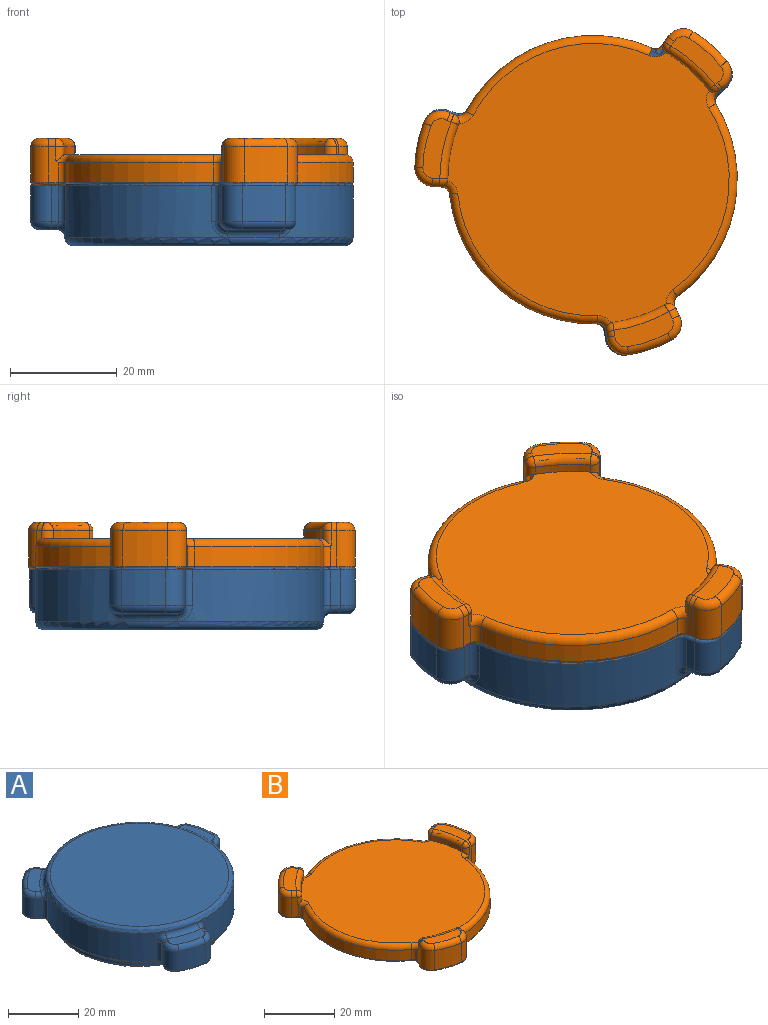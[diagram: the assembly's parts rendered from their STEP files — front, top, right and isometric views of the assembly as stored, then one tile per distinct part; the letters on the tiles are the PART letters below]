
ASSEMBLY  parts=2 mates=1
PART A: 103 faces, bbox 63x62.5x14.7 mm
  f0: cylinder r=27mm len=39.91mm, axis (0,0,1), area 396.5mm2, adj f45,f68,f69,f85,f88,f96
  f1: cylinder r=27mm len=38.76mm, axis (0,0,1), area 396.5mm2, adj f56,f73,f76,f92,f93,f96
  f2: plane 6.7x1.76mm, normal (-0.33,0.94,0), area 12.5mm2, adj f3,f54,f73,f74
  f3: cylinder r=3.5mm len=6.7mm, axis (0,0,-1), area 36mm2, adj f2,f4,f52,f72
  f4: cylinder r=24.41mm len=8.27mm, axis (0,0,-1), area 56.9mm2, adj f3,f5,f50,f75
  f5: cylinder r=3.5mm len=6.7mm, axis (0,0,-1), area 40.2mm2, adj f4,f6,f48,f77
  f6: plane 6.7x1.25mm, normal (0.08,-1,0), area 8.4mm2, adj f5,f46,f79,f81
  f7: plane 11.21x5.6mm, normal (0,0,1), area 38.3mm2, adj f72,f74,f75,f77,f78,f79
  f8: plane 60x59.37mm, normal (0,0,-1), area 386.4mm2, adj f26,f39,f40,f41,f42,f43,f44,f45
  f9: cylinder r=2.15mm len=8mm, axis (0,0,-1), area 108.1mm2, adj f10,f98
  f10: plane 4.3x4.3mm, normal (0,0,-1), area 14.5mm2, adj f9
  f11: cylinder r=2.15mm len=8mm, axis (0,0,-1), area 108.1mm2, adj f12,f97
  f12: plane 4.3x4.3mm, normal (0,0,-1), area 14.5mm2, adj f11
  f13: cylinder r=27mm len=30.36mm, axis (0,0,1), area 396.5mm2, adj f44,f61,f64,f80,f81,f96
  f14: plane 6.7x1.41mm, normal (-0.65,-0.76,0), area 12.5mm2, adj f15,f47,f85,f86
  f15: cylinder r=3.5mm len=6.7mm, axis (0,0,-1), area 36mm2, adj f14,f16,f49,f84
  f16: cylinder r=24.41mm len=6.7mm, axis (0,0,-1), area 56.9mm2, adj f15,f17,f51,f87
  f17: cylinder r=3.5mm len=6.7mm, axis (0,0,-1), area 40.2mm2, adj f16,f18,f53,f89
  f18: plane 6.7x1.04mm, normal (0.83,0.56,0), area 8.4mm2, adj f17,f55,f91,f93
  f19: plane 9.91x9.39mm, normal (0,0,1), area 38.3mm2, adj f84,f86,f87,f89,f90,f91
  f20: cylinder r=2.15mm len=8mm, axis (0,0,-1), area 108.1mm2, adj f21,f101
  f21: plane 4.3x4.3mm, normal (0,0,-1), area 14.5mm2, adj f20
  f22: cylinder r=2.15mm len=8mm, axis (0,0,-1), area 108.1mm2, adj f23,f102
  f23: plane 4.3x4.3mm, normal (0,0,-1), area 14.5mm2, adj f22
  f24: cylinder r=23mm len=46mm, axis (0,0,1), area 1242.8mm2, adj f57,f95
  f25: plane 49x49mm, normal (0,0,-1), area 150.8mm2, adj f57,f58
  f26: cylinder r=25mm len=50mm, axis (0,0,1), area 392.7mm2, adj f8,f58
  f27: plane 51x51mm, normal (0,0,1), area 2042.8mm2, adj f96
  f28: plane 40x40mm, normal (0,0,-1), area 1256.6mm2, adj f95
  f29: plane 6.7x1.83mm, normal (0.98,-0.19,0), area 12.5mm2, adj f30,f42,f61,f62
  f30: cylinder r=3.5mm len=6.7mm, axis (0,0,-1), area 36mm2, adj f29,f31,f40,f60
  f31: cylinder r=24.41mm len=8.04mm, axis (0,0,-1), area 56.9mm2, adj f30,f32,f39,f63
  f32: cylinder r=3.5mm len=6.7mm, axis (0,0,-1), area 40.2mm2, adj f31,f33,f41,f65
  f33: plane 6.7x1.13mm, normal (-0.9,0.43,0), area 8.4mm2, adj f32,f43,f67,f69
  f34: plane 11.2x6.49mm, normal (0,0,1), area 38.3mm2, adj f60,f62,f63,f65,f66,f67
  f35: cylinder r=2.15mm len=8mm, axis (0,0,-1), area 108.1mm2, adj f36,f100
  f36: plane 4.3x4.3mm, normal (0,0,-1), area 14.5mm2, adj f35
  f37: cylinder r=2.15mm len=8mm, axis (0,0,-1), area 108.1mm2, adj f38,f99
  f38: plane 4.3x4.3mm, normal (0,0,-1), area 14.5mm2, adj f37
  f39: torus R=23.91mm, axis (0,0,-1), area 6.6mm2, adj f8,f31,f40,f41
  f40: torus R=3mm, axis (0,0,-1), area 4mm2, adj f8,f30,f39,f42
  f41: torus R=3mm, axis (0,0,-1), area 4.5mm2, adj f8,f32,f39,f43
  f42: cylinder r=0.5mm len=3.64mm, axis (-0.19,-0.98,0), area 2.1mm2, adj f8,f29,f40,f59
  f43: cylinder r=0.5mm len=2.96mm, axis (0.43,0.9,0), area 1.7mm2, adj f8,f33,f41,f70
  f44: torus R=26.5mm, axis (0,0,-1), area 32.9mm2, adj f8,f13,f59,f82
  f45: torus R=26.5mm, axis (0,0,-1), area 32.9mm2, adj f0,f8,f70,f83
  f46: cylinder r=0.5mm len=3.08mm, axis (-1,-0.08,0), area 1.7mm2, adj f6,f8,f48,f82
  f47: cylinder r=0.5mm len=3.06mm, axis (-0.76,0.65,0), area 2.1mm2, adj f8,f14,f49,f83
  f48: torus R=3mm, axis (0,0,-1), area 4.5mm2, adj f5,f8,f46,f50
  f49: torus R=3mm, axis (0,0,-1), area 4mm2, adj f8,f15,f47,f51
  f50: torus R=23.91mm, axis (0,0,-1), area 6.6mm2, adj f4,f8,f48,f52
  f51: torus R=23.91mm, axis (0,0,-1), area 6.6mm2, adj f8,f16,f49,f53
  f52: torus R=3mm, axis (0,0,-1), area 4mm2, adj f3,f8,f50,f54
  f53: torus R=3mm, axis (0,0,-1), area 4.5mm2, adj f8,f17,f51,f55
  f54: cylinder r=0.5mm len=3.57mm, axis (0.94,0.33,0), area 2.1mm2, adj f2,f8,f52,f71
  f55: cylinder r=0.5mm len=2.8mm, axis (0.56,-0.83,0), area 1.7mm2, adj f8,f18,f53,f94
  f56: torus R=26.5mm, axis (0,0,-1), area 32.9mm2, adj f1,f8,f71,f94
  f57: torus R=23.5mm, axis (0,0,-1), area 114.4mm2, adj f24,f25
  f58: torus R=24.5mm, axis (0,0,-1), area 122.5mm2, adj f25,f26
  f59: bspline ~1.81x1.67mm, area 1.4mm2, adj f42,f44,f61
  f60: torus R=2mm, axis (0,0,-1), area 10.7mm2, adj f30,f34,f62,f63
  f61: cylinder r=1.5mm len=6.7mm, axis (0,0,1), area 14.1mm2, adj f13,f29,f59,f64
  f62: cylinder r=1.5mm len=2.11mm, axis (0.19,0.98,0), area 4mm2, adj f29,f34,f60,f64
  f63: torus R=22.91mm, axis (0,0,-1), area 19.6mm2, adj f31,f34,f60,f65
  f64: bspline ~3.52x3.48mm, area 7.1mm2, adj f13,f61,f62,f66
  f65: torus R=2mm, axis (0,0,-1), area 12.1mm2, adj f32,f34,f63,f67
  f66: torus R=28.5mm, axis (0,0,-1), area 24.8mm2, adj f34,f64,f68,f96
  f67: cylinder r=1.5mm len=1.96mm, axis (-0.43,-0.9,0), area 2.7mm2, adj f33,f34,f65,f68
  f68: bspline ~3.67x2.96mm, area 7.1mm2, adj f0,f66,f67,f69
  f69: cylinder r=1.5mm len=6.7mm, axis (0,0,1), area 14.1mm2, adj f0,f33,f68,f70
  f70: bspline ~1.88x1.7mm, area 1.4mm2, adj f43,f45,f69
  f71: bspline ~1.81x1.74mm, area 1.4mm2, adj f54,f56,f73
  f72: torus R=2mm, axis (0,0,-1), area 10.7mm2, adj f3,f7,f74,f75
  f73: cylinder r=1.5mm len=6.7mm, axis (0,0,1), area 14.1mm2, adj f1,f2,f71,f76
  f74: cylinder r=1.5mm len=2.26mm, axis (-0.94,-0.33,0), area 4mm2, adj f2,f7,f72,f76
  f75: torus R=22.91mm, axis (0,0,-1), area 19.6mm2, adj f4,f7,f72,f77
  f76: bspline ~3.52x3.16mm, area 7.1mm2, adj f1,f73,f74,f78
  f77: torus R=2mm, axis (0,0,-1), area 12.1mm2, adj f5,f7,f75,f79
  f78: torus R=28.5mm, axis (0,0,-1), area 24.8mm2, adj f7,f76,f80,f96
  f79: cylinder r=1.5mm len=1.6mm, axis (1,0.08,0), area 2.7mm2, adj f6,f7,f77,f80
  f80: bspline ~3.67x3.33mm, area 7.1mm2, adj f13,f78,f79,f81
  f81: cylinder r=1.5mm len=6.7mm, axis (0,0,1), area 14.1mm2, adj f6,f13,f80,f82
  f82: bspline ~1.78x1.73mm, area 0.7mm2, adj f44,f46,f81
  f83: bspline ~1.91x1.65mm, area 0.7mm2, adj f45,f47,f85
  f84: torus R=2mm, axis (0,0,-1), area 10.7mm2, adj f15,f19,f86,f87
  f85: cylinder r=1.5mm len=6.7mm, axis (0,0,1), area 14.1mm2, adj f0,f14,f83,f88
  f86: cylinder r=1.5mm len=2.39mm, axis (0.76,-0.65,0), area 4mm2, adj f14,f19,f84,f88
  f87: torus R=22.91mm, axis (0,0,-1), area 19.6mm2, adj f16,f19,f84,f89
  f88: bspline ~3.55x3.52mm, area 7.1mm2, adj f0,f85,f86,f90
  f89: torus R=2mm, axis (0,0,-1), area 12.1mm2, adj f17,f19,f87,f91
  f90: torus R=28.5mm, axis (0,0,-1), area 24.8mm2, adj f19,f88,f92,f96
  f91: cylinder r=1.5mm len=2.03mm, axis (-0.56,0.83,0), area 2.7mm2, adj f18,f19,f89,f92
  f92: bspline ~3.67x3.52mm, area 7.1mm2, adj f1,f90,f91,f93
  f93: cylinder r=1.5mm len=6.7mm, axis (0,0,1), area 14.1mm2, adj f1,f18,f92,f94
  f94: bspline ~1.87x1.73mm, area 1.4mm2, adj f55,f56,f93
  f95: torus R=20mm, axis (0,0,1), area 648.7mm2, adj f24,f28
  f96: torus R=25.5mm, axis (0,0,1), area 391.6mm2, adj f0,f1,f13,f27,f66,f78,f90
  f97: torus R=2.35mm, axis (0,0,-1), area 4.4mm2, adj f8,f11
  f98: torus R=2.35mm, axis (0,0,-1), area 4.4mm2, adj f8,f9
  f99: torus R=2.35mm, axis (0,0,-1), area 4.4mm2, adj f8,f37
  f100: torus R=2.35mm, axis (0,0,-1), area 4.4mm2, adj f8,f35
  f101: torus R=2.35mm, axis (0,0,-1), area 4.4mm2, adj f8,f20
  f102: torus R=2.35mm, axis (0,0,-1), area 4.4mm2, adj f8,f22
PART B: 117 faces, bbox 63x62.5x8.7 mm
  f0: cylinder r=27mm len=27.4mm, axis (0,0,1), area 145.8mm2, adj f41,f44,f46,f61
  f1: cylinder r=27mm len=34.99mm, axis (0,0,1), area 145.8mm2, adj f55,f58,f60,f77
  f2: plane 49.6x49.6mm, normal (0,0,-1), area 1932.2mm2, adj f85
  f3: cylinder r=25.3mm len=50.6mm, axis (0,0,1), area 317.9mm2, adj f85,f86
  f4: plane 60x59.37mm, normal (0,0,-1), area 262.4mm2, adj f61,f62,f63,f64,f65,f66,f67,f68
  f5: cylinder r=27mm len=36.02mm, axis (0,0,1), area 145.8mm2, adj f47,f50,f53,f76
  f6: plane 52.72x52.72mm, normal (0,0,1), area 2103.6mm2, adj f7,f18,f29,f40,f42,f43,f44,f45
  f7: cylinder r=27mm len=7.64mm, axis (0,0,-1), area 16.5mm2, adj f6,f48,f54,f93
  f8: plane 6.7x1.42mm, normal (-0.65,-0.76,0), area 11.5mm2, adj f9,f47,f48,f49,f80,f92
  f9: cylinder r=3.5mm len=6.7mm, axis (0,0,-1), area 36mm2, adj f8,f10,f82,f90
  f10: cylinder r=24.41mm len=6.7mm, axis (0,0,-1), area 56.9mm2, adj f9,f11,f84,f88
  f11: cylinder r=3.5mm len=6.7mm, axis (0,0,-1), area 40.2mm2, adj f10,f12,f83,f87
  f12: plane 6.7x1.04mm, normal (0.83,0.56,0), area 7.4mm2, adj f11,f54,f55,f56,f81,f89
  f13: plane 9.91x9.39mm, normal (0,0,1), area 38.3mm2, adj f87,f88,f89,f90,f92,f93
  f14: cylinder r=2.15mm len=8mm, axis (0,0,-1), area 108.1mm2, adj f15,f116
  f15: plane 4.3x4.3mm, normal (0,0,-1), area 14.5mm2, adj f14
  f16: cylinder r=2.15mm len=8mm, axis (0,0,-1), area 108.1mm2, adj f17,f115
  f17: plane 4.3x4.3mm, normal (0,0,-1), area 14.5mm2, adj f16
  f18: cylinder r=27.2mm len=10.1mm, axis (0,0,-1), area 16.6mm2, adj f6,f40,f57,f100
  f19: plane 6.71x1.77mm, normal (-0.33,0.94,0), area 10.9mm2, adj f20,f57,f59,f60,f73,f96
  f20: cylinder r=3.5mm len=6.7mm, axis (0,0,-1), area 36mm2, adj f19,f21,f71,f95
  f21: cylinder r=24.41mm len=8.27mm, axis (0,0,-1), area 56.9mm2, adj f20,f22,f69,f97
  f22: cylinder r=3.5mm len=6.7mm, axis (0,0,-1), area 40.2mm2, adj f21,f23,f67,f99
  f23: plane 6.71x1.26mm, normal (0.08,-1,0), area 6.9mm2, adj f22,f40,f41,f42,f65,f101
  f24: plane 11.2x5.42mm, normal (0,0,1), area 36.2mm2, adj f95,f96,f97,f99,f100,f101
  f25: cylinder r=2.15mm len=8mm, axis (0,0,-1), area 108.1mm2, adj f26,f112
  f26: plane 4.3x4.3mm, normal (0,0,-1), area 14.5mm2, adj f25
  f27: cylinder r=2.15mm len=8mm, axis (0,0,-1), area 108.1mm2, adj f28,f111
  f28: plane 4.3x4.3mm, normal (0,0,-1), area 14.5mm2, adj f27
  f29: cylinder r=27.4mm len=9.86mm, axis (0,0,-1), area 16.7mm2, adj f6,f43,f51,f108
  f30: plane 6.73x1.86mm, normal (0.98,-0.19,0), area 10.4mm2, adj f31,f43,f45,f46,f64,f104
  f31: cylinder r=3.5mm len=6.7mm, axis (0,0,-1), area 36mm2, adj f30,f32,f66,f103
  f32: cylinder r=24.41mm len=8.04mm, axis (0,0,-1), area 56.9mm2, adj f31,f33,f68,f105
  f33: cylinder r=3.5mm len=6.7mm, axis (0,0,-1), area 40.2mm2, adj f32,f34,f70,f107
  f34: plane 6.73x1.16mm, normal (-0.9,0.43,0), area 6.4mm2, adj f33,f51,f52,f53,f72,f109
  f35: plane 11.13x6.12mm, normal (0,0,1), area 34mm2, adj f103,f104,f105,f107,f108,f109
  f36: cylinder r=2.15mm len=8mm, axis (0,0,-1), area 108.1mm2, adj f37,f114
  f37: plane 4.3x4.3mm, normal (0,0,-1), area 14.5mm2, adj f36
  f38: cylinder r=2.15mm len=8mm, axis (0,0,-1), area 108.1mm2, adj f39,f113
  f39: plane 4.3x4.3mm, normal (0,0,-1), area 14.5mm2, adj f38
  f40: cylinder r=1.5mm len=2.72mm, axis (0,0,-1), area 5mm2, adj f6,f18,f23,f42,f102
  f41: cylinder r=1.5mm len=3.6mm, axis (0,0,1), area 7.6mm2, adj f0,f23,f42,f63
  f42: torus R=3mm, axis (0,0,1), area 5.8mm2, adj f6,f23,f40,f41,f44
  f43: cylinder r=1.5mm len=2.58mm, axis (0,0,-1), area 5mm2, adj f6,f29,f30,f45,f106
  f44: torus R=25.5mm, axis (0,0,1), area 93.5mm2, adj f0,f6,f42,f45
  f45: torus R=3mm, axis (0,0,1), area 6.2mm2, adj f6,f30,f43,f44,f46
  f46: cylinder r=1.5mm len=3.6mm, axis (0,0,1), area 7.6mm2, adj f0,f30,f45,f62
  f47: cylinder r=1.5mm len=3.6mm, axis (0,0,1), area 7.6mm2, adj f5,f8,f49,f78
  f48: cylinder r=1.5mm len=2.86mm, axis (0,0,-1), area 5mm2, adj f6,f7,f8,f49,f94
  f49: torus R=3mm, axis (0,0,1), area 5.4mm2, adj f6,f8,f47,f48,f50
  f50: torus R=25.5mm, axis (0,0,1), area 93.5mm2, adj f5,f6,f49,f52
  f51: cylinder r=1.5mm len=2.59mm, axis (0,0,-1), area 5mm2, adj f6,f29,f34,f52,f110
  f52: torus R=3mm, axis (0,0,1), area 6.2mm2, adj f6,f34,f50,f51,f53
  f53: cylinder r=1.5mm len=3.6mm, axis (0,0,1), area 7.6mm2, adj f5,f34,f52,f74
  f54: cylinder r=1.5mm len=2.86mm, axis (0,0,-1), area 5mm2, adj f6,f7,f12,f56,f91
  f55: cylinder r=1.5mm len=3.6mm, axis (0,0,1), area 7.6mm2, adj f1,f12,f56,f79
  f56: torus R=3mm, axis (0,0,1), area 5.4mm2, adj f6,f12,f54,f55,f58
  f57: cylinder r=1.5mm len=2.72mm, axis (0,0,-1), area 5mm2, adj f6,f18,f19,f59,f98
  f58: torus R=25.5mm, axis (0,0,1), area 93.5mm2, adj f1,f6,f56,f59
  f59: torus R=3mm, axis (0,0,1), area 5.8mm2, adj f6,f19,f57,f58,f60
  f60: cylinder r=1.5mm len=3.6mm, axis (0,0,1), area 7.6mm2, adj f1,f19,f59,f75
  f61: torus R=26.5mm, axis (0,0,1), area 31.6mm2, adj f0,f4,f62,f63
  f62: torus R=2mm, axis (0,0,1), area 1.9mm2, adj f4,f46,f61,f64
  f63: torus R=2mm, axis (0,0,1), area 1.9mm2, adj f4,f41,f61,f65
  f64: cylinder r=0.5mm len=1.93mm, axis (0.19,0.98,0), area 1.5mm2, adj f4,f30,f62,f66
  f65: cylinder r=0.5mm len=1.33mm, axis (1,0.08,0), area 1mm2, adj f4,f23,f63,f67
  f66: torus R=3mm, axis (0,0,1), area 4mm2, adj f4,f31,f64,f68
  f67: torus R=3mm, axis (0,0,1), area 4.5mm2, adj f4,f22,f65,f69
  f68: torus R=23.91mm, axis (0,0,1), area 6.6mm2, adj f4,f32,f66,f70
  f69: torus R=23.91mm, axis (0,0,1), area 6.6mm2, adj f4,f21,f67,f71
  f70: torus R=3mm, axis (0,0,1), area 4.5mm2, adj f4,f33,f68,f72
  f71: torus R=3mm, axis (0,0,1), area 4mm2, adj f4,f20,f69,f73
  f72: cylinder r=0.5mm len=1.39mm, axis (-0.43,-0.9,0), area 1mm2, adj f4,f34,f70,f74
  f73: cylinder r=0.5mm len=1.93mm, axis (-0.94,-0.33,0), area 1.5mm2, adj f4,f19,f71,f75
  f74: torus R=2mm, axis (0,0,1), area 1.9mm2, adj f4,f53,f72,f76
  f75: torus R=2mm, axis (0,0,1), area 1.9mm2, adj f4,f60,f73,f77
  f76: torus R=26.5mm, axis (0,0,1), area 31.6mm2, adj f4,f5,f74,f78
  f77: torus R=26.5mm, axis (0,0,1), area 31.6mm2, adj f1,f4,f75,f79
  f78: torus R=2mm, axis (0,0,1), area 1.9mm2, adj f4,f47,f76,f80
  f79: torus R=2mm, axis (0,0,1), area 1.9mm2, adj f4,f55,f77,f81
  f80: cylinder r=0.5mm len=1.74mm, axis (0.76,-0.65,0), area 1.5mm2, adj f4,f8,f78,f82
  f81: cylinder r=0.5mm len=1.36mm, axis (-0.56,0.83,0), area 1mm2, adj f4,f12,f79,f83
  f82: torus R=3mm, axis (0,0,1), area 4mm2, adj f4,f9,f80,f84
  f83: torus R=3mm, axis (0,0,1), area 4.5mm2, adj f4,f11,f81,f84
  f84: torus R=23.91mm, axis (0,0,1), area 6.6mm2, adj f4,f10,f82,f83
  f85: torus R=24.8mm, axis (0,0,1), area 124mm2, adj f2,f3
  f86: torus R=25.8mm, axis (0,0,1), area 125.7mm2, adj f3,f4
  f87: torus R=2mm, axis (0,0,-1), area 12.1mm2, adj f11,f13,f88,f89
  f88: torus R=22.91mm, axis (0,0,-1), area 19.6mm2, adj f10,f13,f87,f90
  f89: cylinder r=1.5mm len=1.84mm, axis (-0.56,0.83,0), area 2.3mm2, adj f12,f13,f87,f91
  f90: torus R=2mm, axis (0,0,-1), area 10.7mm2, adj f9,f13,f88,f92
  f91: sphere r=1.5mm, area 3.7mm2, adj f54,f89,f93
  f92: cylinder r=1.5mm len=2.13mm, axis (0.76,-0.65,0), area 3.6mm2, adj f8,f13,f90,f94
  f93: torus R=28.5mm, axis (0,0,-1), area 24.8mm2, adj f7,f13,f91,f94
  f94: sphere r=1.5mm, area 3.7mm2, adj f48,f92,f93
  f95: torus R=2mm, axis (0,0,-1), area 10.7mm2, adj f20,f24,f96,f97
  f96: cylinder r=1.5mm len=1.85mm, axis (-0.94,-0.33,0), area 3.1mm2, adj f19,f24,f95,f98
  f97: torus R=22.91mm, axis (0,0,-1), area 19.6mm2, adj f21,f24,f95,f99
  f98: sphere r=1.5mm, area 3.7mm2, adj f57,f96,f100
  f99: torus R=2mm, axis (0,0,-1), area 12.1mm2, adj f22,f24,f97,f101
  f100: torus R=28.7mm, axis (0,0,-1), area 24.9mm2, adj f18,f24,f98,f102
  f101: cylinder r=1.5mm len=1.56mm, axis (1,0.08,0), area 1.9mm2, adj f23,f24,f99,f102
  f102: sphere r=1.5mm, area 3.6mm2, adj f40,f100,f101
  f103: torus R=2mm, axis (0,0,-1), area 10.7mm2, adj f31,f35,f104,f105
  f104: cylinder r=1.5mm len=1.68mm, axis (0.19,0.98,0), area 2.6mm2, adj f30,f35,f103,f106
  f105: torus R=22.91mm, axis (0,0,-1), area 19.6mm2, adj f32,f35,f103,f107
  f106: sphere r=1.5mm, area 3.7mm2, adj f43,f104,f108
  f107: torus R=2mm, axis (0,0,-1), area 12.1mm2, adj f33,f35,f105,f109
  f108: torus R=28.9mm, axis (0,0,-1), area 25.1mm2, adj f29,f35,f106,f110
  f109: cylinder r=1.5mm len=1.64mm, axis (-0.43,-0.9,0), area 1.4mm2, adj f34,f35,f107,f110
  f110: sphere r=1.5mm, area 3.7mm2, adj f51,f108,f109
  f111: torus R=2.35mm, axis (0,0,1), area 4.4mm2, adj f4,f27
  f112: torus R=2.35mm, axis (0,0,1), area 4.4mm2, adj f4,f25
  f113: torus R=2.35mm, axis (0,0,1), area 4.4mm2, adj f4,f38
  f114: torus R=2.35mm, axis (0,0,1), area 4.4mm2, adj f4,f36
  f115: torus R=2.35mm, axis (0,0,1), area 4.4mm2, adj f4,f16
  f116: torus R=2.35mm, axis (0,0,1), area 4.4mm2, adj f4,f14
PLACE A rot(axis=(0,-1,0),180deg) t=(-9.91,-23.87,-28.65)mm
PLACE B rot(axis=(0,0,1),156.9deg) t=(-9.91,-23.87,-20.27)mm
MATE cylindrical B.f0 <-> A.f0  axis (0,0,-1) through (-9.91,-23.87,-16.87)mm
